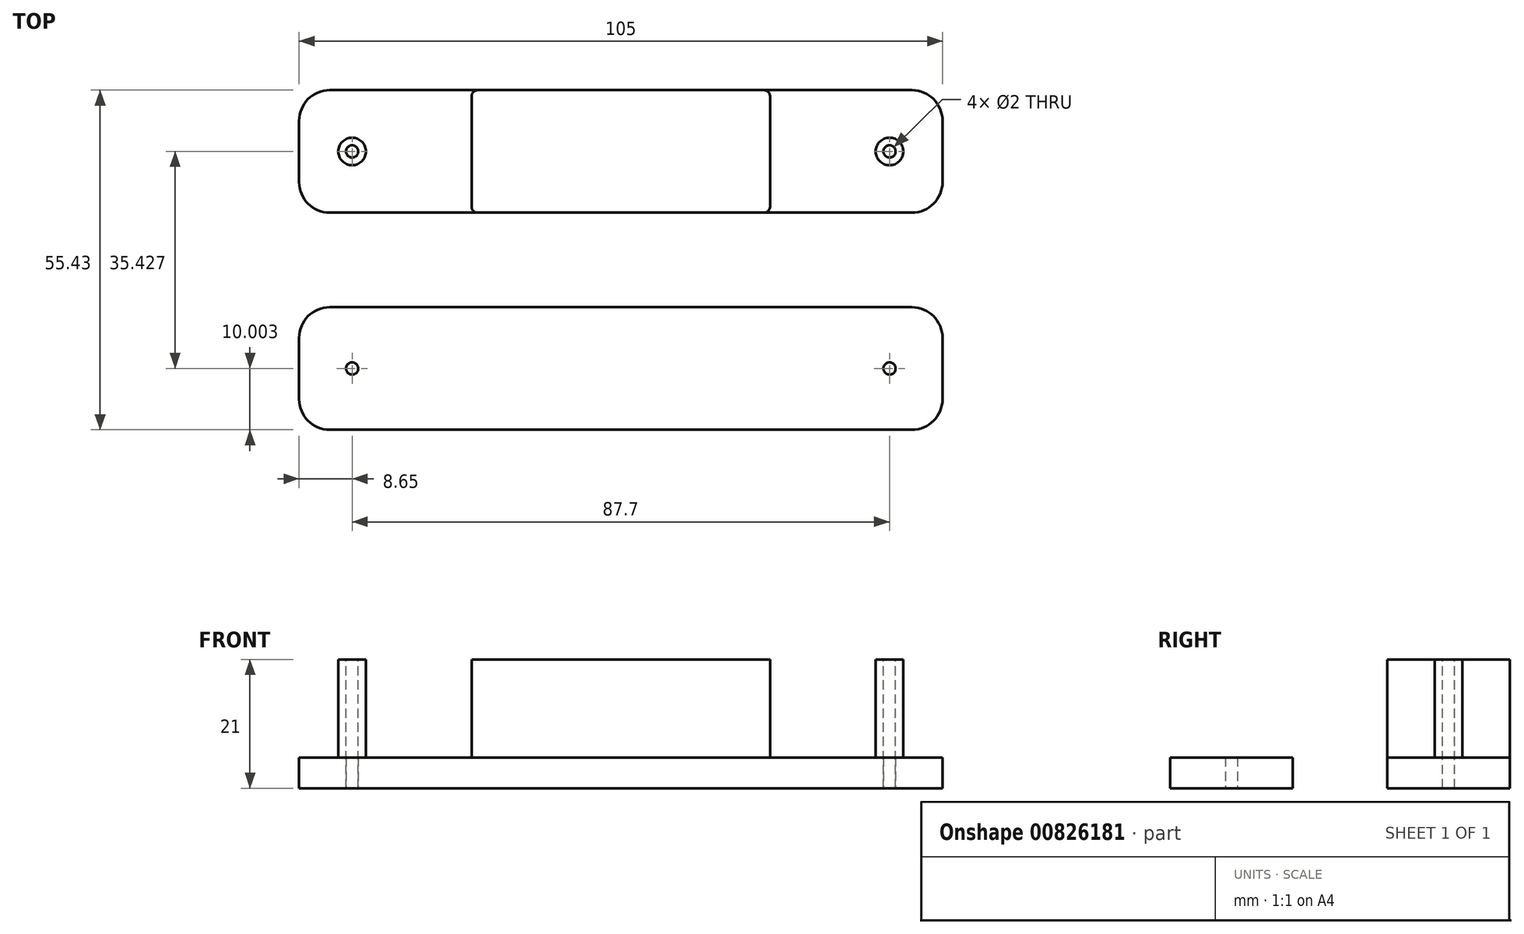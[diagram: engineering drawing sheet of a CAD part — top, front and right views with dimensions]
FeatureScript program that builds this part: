
annotation { "Feature Type Name" : "Feature", "Feature Type Description" : "" }
export const myFeature = defineFeature(function(context is Context, id is Id, definition is map)
    precondition{}
    {
        {
            var Q0;
            Q0=qCreatedBy(makeId("Top.planeOp"),FACE);
            var sketch = newSketch(context, id + "F0", { "sketchPlane" : qUnion([Q0])});
            skLineSegment(sketch, "E0.bottom", {"start": v(52.5, -10) * mm, "end": v(-52.5, -10) * mm});
            skLineSegment(sketch, "E0.top", {"start": v(52.5, 10) * mm, "end": v(-52.5, 10) * mm});
            skLineSegment(sketch, "E0.left", {"start": v(52.5, -10) * mm, "end": v(52.5, 10) * mm});
            skLineSegment(sketch, "E0.right", {"start": v(-52.5, -10) * mm, "end": v(-52.5, 10) * mm});
            skPoint(sketch, "E0.middle", {"position": v(0, 0) * mm});
            skCircle(sketch, "E1", {"center": v(43.85, 0) * mm, "radius": 15 * mm});
            skPoint(sketch, "E2", {"position": v(52.5, 0) * mm});
            skLineSegment(sketch, "E3", {"start": v(0, 10) * mm, "end": v(0, -10) * mm, "construction": true});
            skCircle(sketch, "E4", {"center": v(-43.85, 0) * mm, "radius": 15 * mm});
            skCircle(sketch, "E5", {"center": v(-43.85, 0) * mm, "radius": 2.25 * mm});
            skCircle(sketch, "E6", {"center": v(43.85, 0) * mm, "radius": 2.25 * mm});
            skLineSegment(sketch, "E7", {"start": v(-24.35, 10) * mm, "end": v(-24.35, -10) * mm});
            skPoint(sketch, "E8", {"position": v(-24.35, 0) * mm});
            skLineSegment(sketch, "E9", {"start": v(24.35, 10) * mm, "end": v(24.35, -10) * mm});
            skLineSegment(sketch, "E10.bottom", {"start": v(-52.5, -25.43) * mm, "end": v(52.5, -25.43) * mm});
            skLineSegment(sketch, "E10.top", {"start": v(-52.5, -45.43) * mm, "end": v(52.5, -45.43) * mm});
            skLineSegment(sketch, "E10.left", {"start": v(-52.5, -25.43) * mm, "end": v(-52.5, -45.43) * mm});
            skLineSegment(sketch, "E10.right", {"start": v(52.5, -25.43) * mm, "end": v(52.5, -45.43) * mm});
            skLineSegment(sketch, "E11", {"start": v(-52.5, -16.48) * mm, "end": v(52.5, -16.48) * mm, "construction": true});
            skPoint(sketch, "E12", {"position": v(-52.5, -35.43) * mm});
            skCircle(sketch, "E13", {"center": v(-43.85, -35.43) * mm, "radius": 1 * mm});
            skLineSegment(sketch, "E14", {"start": v(0, -25.43) * mm, "end": v(0, -45.43) * mm});
            skCircle(sketch, "E15", {"center": v(43.85, -35.43) * mm, "radius": 1 * mm});
            skSolve(sketch);
        }
        {
            var Q0;
            {var subQ0=sQuery(id+"F0.wireOp",EDGE,"E7");Q0=makeQuery(id+"F0.imprint","IMPRINT",FACE,{"disambiguationData":[TD([[makeQuery(id+"F0.imprint","IMPRINT",EDGE,{"derivedFrom":subQ0}),1.0]])]});}
            extrude(context, id + "F1", {"entities" : qUnion([Q0]), "depth" : 21 * mm, "offsetDistance" : 25 * mm});
        }
        {
            var Q0;
            Q0=makeQuery(id+"F0.imprint","IMPRINT",FACE,{"disambiguationData":[TD([[makeQuery(id+"F0.imprint","IMPRINT",EDGE,{"derivedFrom":sQuery(id+"F0.wireOp",EDGE,"E10.bottom")}),-1.0]])]});
            extrude(context, id + "F2", {"entities" : qUnion([Q0]), "depth" : 5 * mm, "offsetDistance" : 25 * mm});
        }
        {
            var Q0;
            {var subQ5=sQuery(id+"F0.wireOp",EDGE,"E0.right");Q0=makeQuery(id+"F0.imprint","IMPRINT",FACE,{"disambiguationData":[TD([[makeQuery(id+"F0.imprint","IMPRINT",EDGE,{"derivedFrom":subQ5}),-1.0]])]});}
            var Q1;
            {var subQ0=sQuery(id+"F0.wireOp",EDGE,"E7");Q1=makeQuery(id+"F0.imprint","IMPRINT",FACE,{"disambiguationData":[TD([[makeQuery(id+"F0.imprint","IMPRINT",EDGE,{"derivedFrom":subQ0}),-1.0]])]});}
            var Q2;
            {var subQ5=sQuery(id+"F0.wireOp",EDGE,"E0.left");Q2=makeQuery(id+"F0.imprint","IMPRINT",FACE,{"disambiguationData":[TD([[makeQuery(id+"F0.imprint","IMPRINT",EDGE,{"derivedFrom":subQ5}),1.0]])]});}
            var Q3;
            {var subQ0=sQuery(id+"F0.wireOp",EDGE,"E9");Q3=makeQuery(id+"F0.imprint","IMPRINT",FACE,{"disambiguationData":[TD([[makeQuery(id+"F0.imprint","IMPRINT",EDGE,{"derivedFrom":subQ0}),1.0]])]});}
            extrude(context, id + "F3", {"entities" : qUnion([Q0, Q1, Q2, Q3]), "operationType" : NewBodyOperationType.ADD, "depth" : 5 * mm, "offsetDistance" : 25 * mm});
        }
        {
            var Q0;
            Q0=makeQuery(id+"F0.imprint","IMPRINT",FACE,{"disambiguationData":[TD([[makeQuery(id+"F0.imprint","IMPRINT",EDGE,{"derivedFrom":sQuery(id+"F0.wireOp",EDGE,"E5")}),1.0]])]});
            var Q1;
            Q1=makeQuery(id+"F0.imprint","IMPRINT",FACE,{"disambiguationData":[TD([[makeQuery(id+"F0.imprint","IMPRINT",EDGE,{"derivedFrom":sQuery(id+"F0.wireOp",EDGE,"E6")}),1.0]])]});
            extrude(context, id + "F4", {"entities" : qUnion([Q0, Q1]), "operationType" : NewBodyOperationType.ADD, "depth" : 21 * mm, "offsetDistance" : 25 * mm});
        }
        {
            var Q0;
            Q0=makeQuery(id+"F3.opExtrude","SWEPT_EDGE",EDGE,{"disambiguationData":[OSD([sQuery(id+"F0.wireOp",EDGE,"E0.bottom"),sQuery(id+"F0.wireOp",EDGE,"E0.right")])]});
            var Q1;
            Q1=makeQuery(id+"F3.opExtrude","SWEPT_EDGE",EDGE,{"disambiguationData":[OSD([sQuery(id+"F0.wireOp",EDGE,"E0.bottom"),sQuery(id+"F0.wireOp",EDGE,"E0.left")])]});
            var Q2;
            Q2=makeQuery(id+"F3.opExtrude","SWEPT_EDGE",EDGE,{"disambiguationData":[OSD([sQuery(id+"F0.wireOp",EDGE,"E0.top"),sQuery(id+"F0.wireOp",EDGE,"E0.left")])]});
            var Q3;
            Q3=makeQuery(id+"F3.opExtrude","SWEPT_EDGE",EDGE,{"disambiguationData":[OSD([sQuery(id+"F0.wireOp",EDGE,"E0.top"),sQuery(id+"F0.wireOp",EDGE,"E0.right")])]});
            var Q4;
            Q4=makeQuery(id+"F2.opExtrude","SWEPT_EDGE",EDGE,{"disambiguationData":[OSD([sQuery(id+"F0.wireOp",EDGE,"E10.top"),sQuery(id+"F0.wireOp",EDGE,"E10.left")])]});
            var Q5;
            Q5=makeQuery(id+"F2.opExtrude","SWEPT_EDGE",EDGE,{"disambiguationData":[OSD([sQuery(id+"F0.wireOp",EDGE,"E10.bottom"),sQuery(id+"F0.wireOp",EDGE,"E10.left")])]});
            var Q6;
            Q6=makeQuery(id+"F2.opExtrude","SWEPT_EDGE",EDGE,{"disambiguationData":[OSD([sQuery(id+"F0.wireOp",EDGE,"E10.top"),sQuery(id+"F0.wireOp",EDGE,"E10.right")])]});
            var Q7;
            Q7=makeQuery(id+"F2.opExtrude","SWEPT_EDGE",EDGE,{"disambiguationData":[OSD([sQuery(id+"F0.wireOp",EDGE,"E10.bottom"),sQuery(id+"F0.wireOp",EDGE,"E10.right")])]});
            fillet(context, id + "F5", {"entities" : qUnion([Q0, Q1, Q2, Q3, Q4, Q5, Q6, Q7]), "radius" : 5 * mm, "tangentPropagation" : true, "allowEdgeOverflow" : false});
        }
        {
            var Q0;
            Q0=makeQuery(id+"F1.opExtrude","SWEPT_EDGE",EDGE,{"disambiguationData":[OSD([sQuery(id+"F0.wireOp",EDGE,"E0.bottom"),sQuery(id+"F0.wireOp",EDGE,"E9")])]});
            var Q1;
            Q1=makeQuery(id+"F1.opExtrude","SWEPT_EDGE",EDGE,{"disambiguationData":[OSD([sQuery(id+"F0.wireOp",EDGE,"E0.top"),sQuery(id+"F0.wireOp",EDGE,"E9")])]});
            var Q2;
            Q2=makeQuery(id+"F1.opExtrude","SWEPT_EDGE",EDGE,{"disambiguationData":[OSD([sQuery(id+"F0.wireOp",EDGE,"E0.bottom"),sQuery(id+"F0.wireOp",EDGE,"E7")])]});
            var Q3;
            Q3=makeQuery(id+"F1.opExtrude","SWEPT_EDGE",EDGE,{"disambiguationData":[OSD([sQuery(id+"F0.wireOp",EDGE,"E0.top"),sQuery(id+"F0.wireOp",EDGE,"E7")])]});
            fillet(context, id + "F6", {"entities" : qUnion([Q0, Q1, Q2, Q3]), "radius" : 1 * mm, "tangentPropagation" : true, "allowEdgeOverflow" : false});
        }
        {
            var Q0;
            Q0=makeQuery(id+"F4.opExtrude","CAP_FACE",FACE,{"disambiguationData":[OSD([sQuery(id+"F0.wireOp",EDGE,"E5")])],"isStart":false});
            var sketch = newSketch(context, id + "F7", { "sketchPlane" : qUnion([Q0])});
            skCircle(sketch, "E16", {"center": v(-43.85, 0) * mm, "radius": 1 * mm});
            skSolve(sketch);
        }
        {
            var Q0;
            Q0=makeQuery(id+"F4.opExtrude","CAP_FACE",FACE,{"disambiguationData":[OSD([sQuery(id+"F0.wireOp",EDGE,"E6")])],"isStart":false});
            var sketch = newSketch(context, id + "F8", { "sketchPlane" : qUnion([Q0])});
            skCircle(sketch, "E17", {"center": v(43.85, 0) * mm, "radius": 1 * mm});
            skSolve(sketch);
        }
        {
            var Q0;
            Q0=makeQuery(id+"F7.imprint","IMPRINT",FACE,{"disambiguationData":[TD([[makeQuery(id+"F7.imprint","IMPRINT",EDGE,{"derivedFrom":sQuery(id+"F7.wireOp",EDGE,"E16")}),1.0]])]});
            var Q1;
            Q1=makeQuery(id+"F8.imprint","IMPRINT",FACE,{"disambiguationData":[TD([[makeQuery(id+"F8.imprint","IMPRINT",EDGE,{"derivedFrom":sQuery(id+"F8.wireOp",EDGE,"E17")}),1.0]])]});
            extrude(context, id + "F9", {"entities" : qUnion([Q0, Q1]), "operationType" : NewBodyOperationType.REMOVE, "oppositeDirection" : true, "depth" : 22.6 * mm, "offsetDistance" : 25 * mm});
        }
    });
